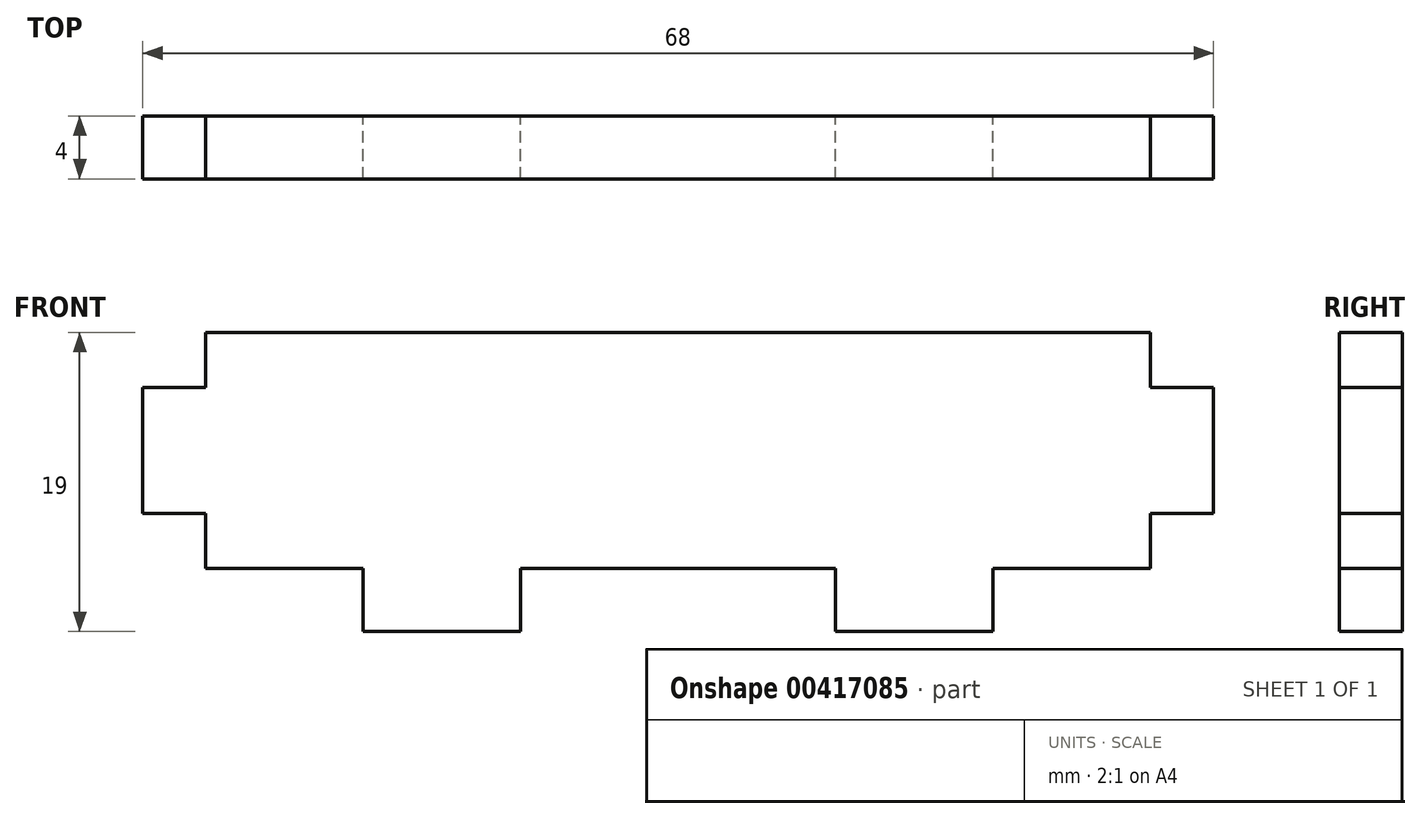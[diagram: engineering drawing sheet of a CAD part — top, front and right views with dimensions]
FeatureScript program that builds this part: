
annotation { "Feature Type Name" : "Feature", "Feature Type Description" : "" }
export const myFeature = defineFeature(function(context is Context, id is Id, definition is map)
    precondition{}
    {
        {
            var Q0;
            Q0=qCreatedBy(makeId("Front.planeOp"),FACE);
            var sketch = newSketch(context, id + "F0", { "sketchPlane" : qUnion([Q0])});
            skLineSegment(sketch, "E0", {"start": v(0, 0) * mm, "end": v(-30, 0) * mm});
            skLineSegment(sketch, "E1", {"start": v(-30, 0) * mm, "end": v(-30, -3.5) * mm});
            skLineSegment(sketch, "E2", {"start": v(-30, -3.5) * mm, "end": v(-34, -3.5) * mm});
            skLineSegment(sketch, "E3", {"start": v(-34, -3.5) * mm, "end": v(-34, -11.5) * mm});
            skLineSegment(sketch, "E4", {"start": v(-34, -11.5) * mm, "end": v(-30, -11.5) * mm});
            skLineSegment(sketch, "E5", {"start": v(-30, -11.5) * mm, "end": v(-30, -15) * mm});
            skLineSegment(sketch, "E6", {"start": v(-30, -15) * mm, "end": v(-20, -15) * mm});
            skLineSegment(sketch, "E7", {"start": v(-20, -15) * mm, "end": v(-20, -19) * mm});
            skLineSegment(sketch, "E8", {"start": v(-20, -19) * mm, "end": v(-10, -19) * mm});
            skLineSegment(sketch, "E9", {"start": v(-10, -19) * mm, "end": v(-10, -15) * mm});
            skLineSegment(sketch, "E10", {"start": v(-10, -15) * mm, "end": v(0, -15) * mm});
            skLineSegment(sketch, "E11.MirrorCS", {"start": v(10, -19) * mm, "end": v(10, -15) * mm});
            skLineSegment(sketch, "E12.MirrorCS", {"start": v(34, -11.5) * mm, "end": v(30, -11.5) * mm});
            skLineSegment(sketch, "E13.MirrorCS", {"start": v(20, -15) * mm, "end": v(20, -19) * mm});
            skLineSegment(sketch, "E14.MirrorCS", {"start": v(30, -3.5) * mm, "end": v(34, -3.5) * mm});
            skLineSegment(sketch, "E15.MirrorCS", {"start": v(0, 0) * mm, "end": v(30, 0) * mm});
            skLineSegment(sketch, "E16.MirrorCS", {"start": v(10, -15) * mm, "end": v(0, -15) * mm});
            skLineSegment(sketch, "E17.MirrorCS", {"start": v(30, 0) * mm, "end": v(30, -3.5) * mm});
            skLineSegment(sketch, "E18.MirrorCS", {"start": v(30, -15) * mm, "end": v(20, -15) * mm});
            skLineSegment(sketch, "E19.MirrorCS", {"start": v(34, -3.5) * mm, "end": v(34, -11.5) * mm});
            skLineSegment(sketch, "E20.MirrorCS", {"start": v(30, -11.5) * mm, "end": v(30, -15) * mm});
            skLineSegment(sketch, "E21.MirrorCS", {"start": v(20, -19) * mm, "end": v(10, -19) * mm});
            skSolve(sketch);
        }
        {
            var Q0;
            Q0=makeQuery(id+"F0.imprint","IMPRINT",FACE,{"disambiguationData":[TD([[makeQuery(id+"F0.imprint","IMPRINT",EDGE,{"derivedFrom":sQuery(id+"F0.wireOp",EDGE,"E0")}),1.0]])]});
            extrude(context, id + "F1", {"entities" : qUnion([Q0]), "depth" : 4 * mm});
        }
    });
